# Revit family: Domotics-DomesticRanges-GEWISS-CHORUS_POWER-SOCKET-OUTLET_ISR_1M
name_source: partatom
category: Apparecchi elettrici
revit_build: Autodesk Revit 2016 (Build: 20161004_0715(x64)
units: mm (PartAtom-declared; Revit-internal decimal feet)

## family parameters
Condiviso = Sì
Host = Superficie
Mantenere orientamento annotazione = Sì
Punto di calcolo locali = Sì
Quota connettore circolare = Usa diametro
Taglio con vuoti quando caricato = Sì
Tipo di parte = Normale

## types (3) — shared parameters
Breaking capacity: = 1.25 In (100 position changes)
Carico apparente = 0 VA
Catalogue = DOMOTICS
Catalogue Range = CHORUS - DOMESTIC RANGE
Category = Socket-outlet
Characteristics = With safety shields
Description. = Socket-outlet
Description: = 2P - 10 A
Electrocod = 0131
For plug pins = Round Ã˜ 4 mm
Glow Wire Test = 850°C
IDF = fbd36d13-40d4-4fd1-bf42-085d66474c4b
IDT = 7facc626-10cf-4a1f-a145-bd78139a884e
Immagine tipo = GW14282.jpg
Insulation resistance = > 5 MOhm
N. poli = 1
No. Chorus modules = 1
No. Chorus modules: = 1
Produttore = GEWISS S.p.A.
Prolonged operation (no.of position changes) = 10.000 at In 250 V ac cosÃ˜=0,8
Prospetto di default = 1219 mm
Resistance at test voltage = 2000 V at 50 Hz for 1 minute
SEO = Socket outlet
Standard = Israeli
Standard: = Israeli
Standard; = IEC 60884-1
TXT ELETTRICO = 10
Technical sheet = https://www.gewiss.com
Terminal grip on cable traction = > 50 N
Terminal tightening capacity flexible cables (mm2) = min. 0,75 - max. 2x4
Terminal tightening capacity rigid cables (mm2) = min. 0,5 - max. 2x2,5
Thermo-pressure with ball = 125
Tipo = CHORUS PRESE ISRAELE 1M_GENERICO : GW14282 Presa 1M 2P 10A standard Israeliano titanio
URL = https://www.gewiss.com
Version file RFA = 19.0
Volt = 230 V
Voltage = 250 V ac
Voltage: = 250 V ac
Wiring terminals = With screw

## per-type parameters (varying)
| type | Colour | Descrizione | EAN code | Modello |
| GW10282 - Socket outlet 1M 2P 10a israeli std white | White | SOCKET-OUTLET 1M 2P 10A ISRAELI STD WH | 8011564815117 | GW10282 |
| GW14282 - Socket outlet 1M 2P 10a israeli std titanium | Titanium | SOCKET-OUTLET 1M 2P 10A ISRAELI STD TI. | 8011564815131 | GW14282 |
| GW12282 - Socket outlet 1M 2P 10a israeli std black | Black | SOCKET-OUTLET 1M 2P 10A ISRAELI STD BL. | 8011564815124 | GW12282 |

note: source unit labels omitted for Thermo-pressure with ball — the stored unit's dimension contradicts the parameter name (converter mislabeling)

## geometry (parser evidence)
native form markers: Sweep x2
no freeform markers — native parametric forms only
